# Revit family: NBS_Allermuir_DmstcChrs_Oran_Sofa
name_source: partatom
category: Furniture
revit_build: Autodesk Revit 2016 (Build: 20161004_0715(x64)
units: mm (PartAtom-declared; Revit-internal decimal feet)

## family parameters
Always vertical = Yes
Cut with Voids When Loaded = No
Room Calculation Point = No
Shared = No
Work Plane-Based = No

## types (3) — shared parameters
AssetType = Moveable
Category = Pr_40_50_12_22:Dining chairs
DurationUnit = year
ExpectedLife = 5
FrameDepth = 910 mm  [stored 2.98556 ft]
FrameMaterials = Aluminium
FramesColour = Black, tusk grey
FramesFinish = Powder coat
IfcExportAs = IfcFurnitureType
IfcExportType = SOFA
IsBuiltIn = No
ManufacturerName = Allermuir
ManufacturerURL = http://www.thesenatorgroup.com
ModelReference = Oran
NBSCertification = www.nationalbimlibrary.com/cert/0nppwlyx
NBSDescription = Domestic chairs
NBSReference = 45-35-20/365
NominalDepth = 947 mm  [stored 3.10696 ft]
NominalHeight = 704 mm  [stored 2.30971 ft]
NominalWidth = 955 mm
SeatFrameMaterial = NBS_Concept
SeatSeatingMaterial = NBS_Concept
SeatingHeight = 440 mm  [stored 1.44357 ft]
SeatsAndBacksFinish = Fully upholstered
Sofa = Yes
Status = UNSET
Uniclass2015Code = Pr_40_50_12_22
Uniclass2015Title = Dining chairs
Uniclass2015Version = Products v1.9
Version = 1
WarrantyDescription = Allermuir warrant that its manufactured products are free from manufacturing defects in materials or workmanship for a period of five years
WarrantyDurationParts = 5
WarrantyDurationUnit = year

## per-type parameters (varying)
| type | BIMObjectName | Cushions200 | Cushions250 | Cushions300 | Description | Features | FrameLength | HighestSeatingHeight | LowestSeatingHeight | MiddleCushion | ModelNumber | Name | NominalLength | Size |
| ORA200 | NBS_Allermuir_DomesticChairs_Oran_ORA200 | Yes | No | No | 2 seat sofa | Fully upholstered, traditional carcass construction, tensioned seat support, feather wrapped sprung seat foam, cast aluminium legs and aluminium perimeter frame finished in black powder coat, curled feather filled cushion with fire retardant inner cover, plastic glides, aluminium frame available in tusk grey powder coat, two-tone upholstery | 1819 mm  [stored 5.96785 ft] | 440 mm  [stored 1.44357 ft] | 440 mm  [stored 1.44357 ft] | No | ORA200 | DomesticChairs_Oran_ORA300_Allermuir | 1859 mm  [stored 6.09908 ft] | 940 x 2599 x 700 mm |
| ORA250 | NBS_Allermuir_DomesticChairs_Oran_ORA250 | No | Yes | No | Arm chair | Fully upholstered, traditional carcass construction, tensioned seat support, feather wrapped sprung seat foam, cast aluminium legs and aluminium perimeter frame finished in black powder coat, curled feather filled cushion with fire retardant inner cover, plastic glides, aluminium frame available in tusk grey powder coat, wo-tone upholstery | 2169 mm  [stored 7.11614 ft] | 440 mm  [stored 1.44357 ft] | 440 mm  [stored 1.44357 ft] | No | ORA100 | DomesticChairs_Oran_ORA250_Allermuir | 2209 mm  [stored 7.24738 ft] | 940 x 2195 x 700 mm |
| ORA300 | NBS_Allermuir_DomesticChairs_Oran_ORA300 | No | No | Yes | 2 seat sofa | Fully upholstered, traditional carcass construction, tensioned seat support, feather wrapped sprung seat foam, cast aluminium legs and aluminium perimeter frame finished in black powder coat, curled feather filled cushion with fire retardant inner cover, plastic glides, aluminium frame available in tusk grey powder coat, two-tone upholstery | 2554 mm  [stored 8.37927 ft] | 0 mm  [stored 0 ft] | 0 mm  [stored 0 ft] | Yes | ORA200 | DomesticChairs_Oran_ORA300_Allermuir | 2594 mm  [stored 8.5105 ft] | 940 x 2599 x 700 mm |

note: [stored X ft] marks values corroborated as IEEE doubles in the binary element streams (Revit-internal decimal feet)

## geometry (parser evidence)
native form markers: Sweep x13
no freeform markers — native parametric forms only
